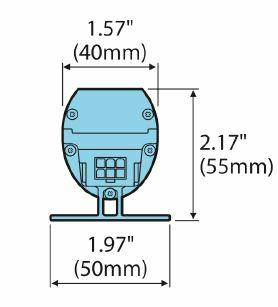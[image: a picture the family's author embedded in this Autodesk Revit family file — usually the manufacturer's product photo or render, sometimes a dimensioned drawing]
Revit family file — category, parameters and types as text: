
# Revit family: Lighting-Linear-Acclaim-XTR
name_source: partatom
category: Lighting Fixtures
units: mm (PartAtom-declared; Revit-internal decimal feet)

## family parameters
Cut with Voids When Loaded = No
Host = Face
Light Source = Yes
Part Type = Normal
Room Calculation Point = No
Round Connector Dimension = Use Diameter
Shared = No

## types (1)
- Lighting-Linear-Acclaim-XTR
    Apparent Load = 0 VA
    Color Filter = 16777215
    Default Elevation = 48 "
    Description = Linear LED
    Dimming Lamp Color Temperature Shift = <None>
    Emit from Line Length = 48 "
    Height = 2.52 "
    Housing Finish = Aluminum
    Lamp = LED
    Length = 48 "
    Manufacturer = Acclaim Lighting
    Model = Linear XTR
    Number of Poles = 1
    Photometric Web File = Load File
    Power Factor = 1
    Tilt Angle = -90.00°
    URL = http://www.acclaimlighting.com
    Voltage = 0 V
    Width = 1.73 "

## geometry (parser evidence)
native form markers: Blend x13, Sweep x2
no freeform markers — native parametric forms only
